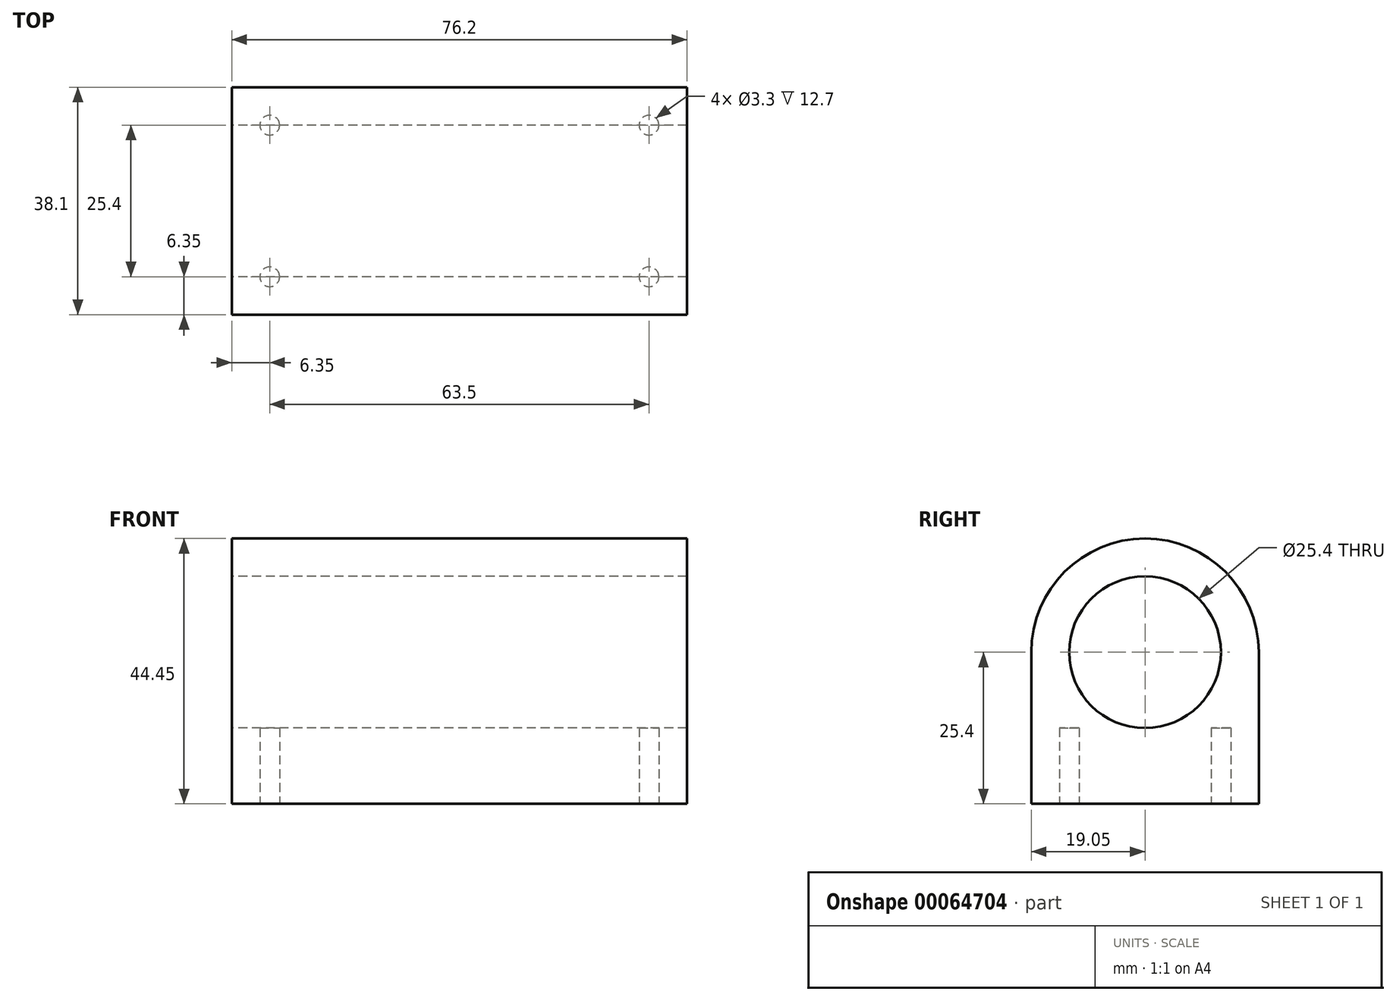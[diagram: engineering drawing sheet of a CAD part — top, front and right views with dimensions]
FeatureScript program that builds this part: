
annotation { "Feature Type Name" : "Feature", "Feature Type Description" : "" }
export const myFeature = defineFeature(function(context is Context, id is Id, definition is map)
    precondition{}
    {
        {
            var Q0;
            Q0=qCreatedBy(makeId("Right.planeOp"),FACE);
            var sketch = newSketch(context, id + "F0", { "sketchPlane" : qUnion([Q0])});
            skCircle(sketch, "E0", {"center": v(0, 0) * mm, "radius": 12.7 * mm});
            skArc(sketch, "E1", {"start": v(19.05, 0) * mm, "mid": v(0, 19.05) * mm, "end": v(-19.05, 0) * mm});
            skLineSegment(sketch, "E2", {"start": v(-19.05, 0) * mm, "end": v(-19.05, -25.4) * mm});
            skLineSegment(sketch, "E3", {"start": v(19.05, 0) * mm, "end": v(19.05, -25.4) * mm});
            skLineSegment(sketch, "E4", {"start": v(19.05, -25.4) * mm, "end": v(-19.05, -25.4) * mm});
            skSolve(sketch);
        }
        {
            var Q0;
            Q0 = qSketchRegion(id + "F0", true);
            extrude(context, id + "F1", {"entities" : qUnion([Q0]), "depth" : 76.2 * mm});
        }
        {
            var Q0;
            Q0=makeQuery(id+"F1.opExtrude","SWEPT_FACE",FACE,{"disambiguationData":[OSD([sQuery(id+"F0.wireOp",EDGE,"E4")])]});
            var sketch = newSketch(context, id + "F2", { "sketchPlane" : qUnion([Q0])});
            skCircle(sketch, "E5", {"center": v(6.35, 12.7) * mm, "radius": 1.65 * mm});
            skCircle(sketch, "E6", {"center": v(6.35, -12.7) * mm, "radius": 1.65 * mm});
            skCircle(sketch, "E7", {"center": v(69.85, 12.7) * mm, "radius": 1.65 * mm});
            skCircle(sketch, "E8", {"center": v(69.85, -12.7) * mm, "radius": 1.65 * mm});
            skSolve(sketch);
        }
        {
            var Q0;
            Q0=makeQuery(id+"F2.imprint","IMPRINT",FACE,{"disambiguationData":[TD([[makeQuery(id+"F2.imprint","IMPRINT",EDGE,{"derivedFrom":sQuery(id+"F2.wireOp",EDGE,"E5")}),1.0]])]});
            var Q1;
            Q1=makeQuery(id+"F2.imprint","IMPRINT",FACE,{"disambiguationData":[TD([[makeQuery(id+"F2.imprint","IMPRINT",EDGE,{"derivedFrom":sQuery(id+"F2.wireOp",EDGE,"E6")}),1.0]])]});
            var Q2;
            Q2=makeQuery(id+"F2.imprint","IMPRINT",FACE,{"disambiguationData":[TD([[makeQuery(id+"F2.imprint","IMPRINT",EDGE,{"derivedFrom":sQuery(id+"F2.wireOp",EDGE,"E7")}),1.0]])]});
            var Q3;
            Q3=makeQuery(id+"F2.imprint","IMPRINT",FACE,{"disambiguationData":[TD([[makeQuery(id+"F2.imprint","IMPRINT",EDGE,{"derivedFrom":sQuery(id+"F2.wireOp",EDGE,"E8")}),1.0]])]});
            extrude(context, id + "F3", {"entities" : qUnion([Q0, Q1, Q2, Q3]), "operationType" : NewBodyOperationType.REMOVE, "oppositeDirection" : true, "depth" : 12.7 * mm});
        }
    });
